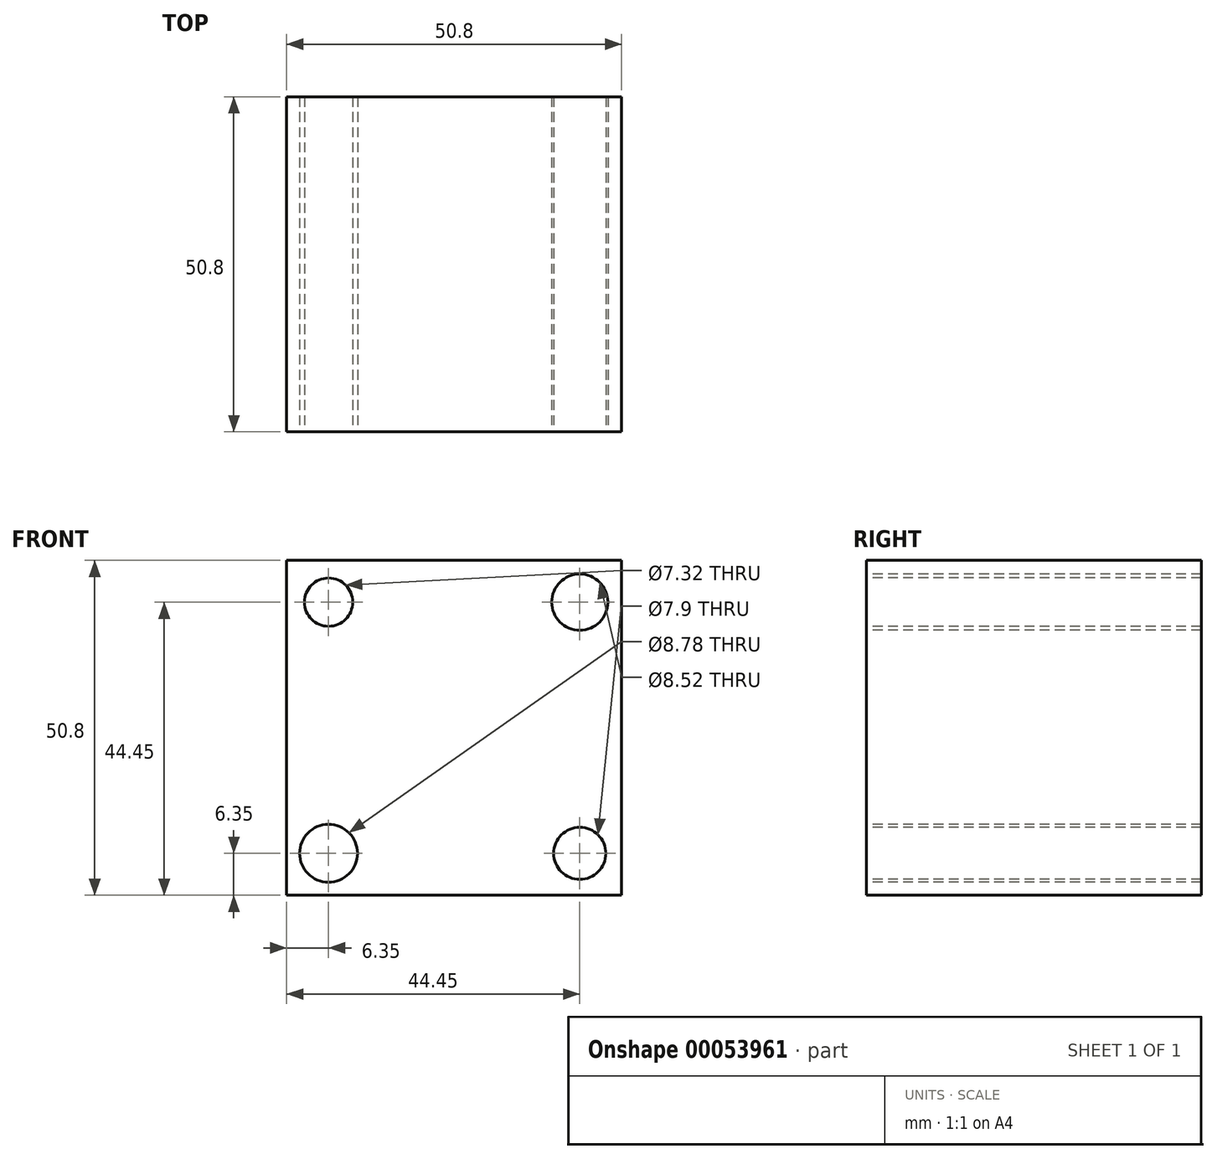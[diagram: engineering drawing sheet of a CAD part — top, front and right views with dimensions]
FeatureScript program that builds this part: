
annotation { "Feature Type Name" : "Feature", "Feature Type Description" : "" }
export const myFeature = defineFeature(function(context is Context, id is Id, definition is map)
    precondition{}
    {
        {
            var Q0;
            Q0=qCreatedBy(makeId("Front.planeOp"),FACE);
            var sketch = newSketch(context, id + "F0", { "sketchPlane" : qUnion([Q0])});
            skLineSegment(sketch, "E0.bottom", {"start": v(0, 0) * mm, "end": v(50.8, 0) * mm});
            skLineSegment(sketch, "E0.top", {"start": v(0, 50.8) * mm, "end": v(50.8, 50.8) * mm});
            skLineSegment(sketch, "E0.left", {"start": v(0, 0) * mm, "end": v(0, 50.8) * mm});
            skLineSegment(sketch, "E0.right", {"start": v(50.8, 0) * mm, "end": v(50.8, 50.8) * mm});
            skSolve(sketch);
        }
        {
            var Q0;
            Q0=makeQuery(id+"F0.imprint","IMPRINT",FACE,{"disambiguationData":[TD([[makeQuery(id+"F0.imprint","IMPRINT",EDGE,{"derivedFrom":sQuery(id+"F0.wireOp",EDGE,"E0.bottom")}),1.0]])]});
            extrude(context, id + "F1", {"entities" : qUnion([Q0]), "depth" : 50.8 * mm});
        }
        {
            var Q0;
            Q0=makeQuery(id+"F1.opExtrude","CAP_FACE",FACE,{"disambiguationData":[OSD([sQuery(id+"F0.wireOp",EDGE,"E0.bottom"),sQuery(id+"F0.wireOp",EDGE,"E0.top"),sQuery(id+"F0.wireOp",EDGE,"E0.left"),sQuery(id+"F0.wireOp",EDGE,"E0.right")])],"isStart":false});
            var sketch = newSketch(context, id + "F2", { "sketchPlane" : qUnion([Q0])});
            skCircle(sketch, "E1", {"center": v(6.35, 44.45) * mm, "radius": 3.66 * mm});
            skCircle(sketch, "E2", {"center": v(44.45, 44.45) * mm, "radius": 4.26 * mm});
            skCircle(sketch, "E3", {"center": v(6.35, 6.35) * mm, "radius": 4.4 * mm});
            skCircle(sketch, "E4", {"center": v(44.45, 6.35) * mm, "radius": 3.95 * mm});
            skSolve(sketch);
        }
        {
            var Q0;
            Q0=makeQuery(id+"F2.imprint","IMPRINT",FACE,{"disambiguationData":[TD([[makeQuery(id+"F2.imprint","IMPRINT",EDGE,{"derivedFrom":sQuery(id+"F2.wireOp",EDGE,"E1")}),1.0]])]});
            var Q1;
            Q1=makeQuery(id+"F2.imprint","IMPRINT",FACE,{"disambiguationData":[TD([[makeQuery(id+"F2.imprint","IMPRINT",EDGE,{"derivedFrom":sQuery(id+"F2.wireOp",EDGE,"E2")}),1.0]])]});
            var Q2;
            Q2=makeQuery(id+"F2.imprint","IMPRINT",FACE,{"disambiguationData":[TD([[makeQuery(id+"F2.imprint","IMPRINT",EDGE,{"derivedFrom":sQuery(id+"F2.wireOp",EDGE,"E3")}),1.0]])]});
            var Q3;
            Q3=makeQuery(id+"F2.imprint","IMPRINT",FACE,{"disambiguationData":[TD([[makeQuery(id+"F2.imprint","IMPRINT",EDGE,{"derivedFrom":sQuery(id+"F2.wireOp",EDGE,"E4")}),1.0]])]});
            extrude(context, id + "F3", {"entities" : qUnion([Q0, Q1, Q2, Q3]), "operationType" : NewBodyOperationType.REMOVE, "oppositeDirection" : true, "depth" : 50.8 * mm});
        }
    });
